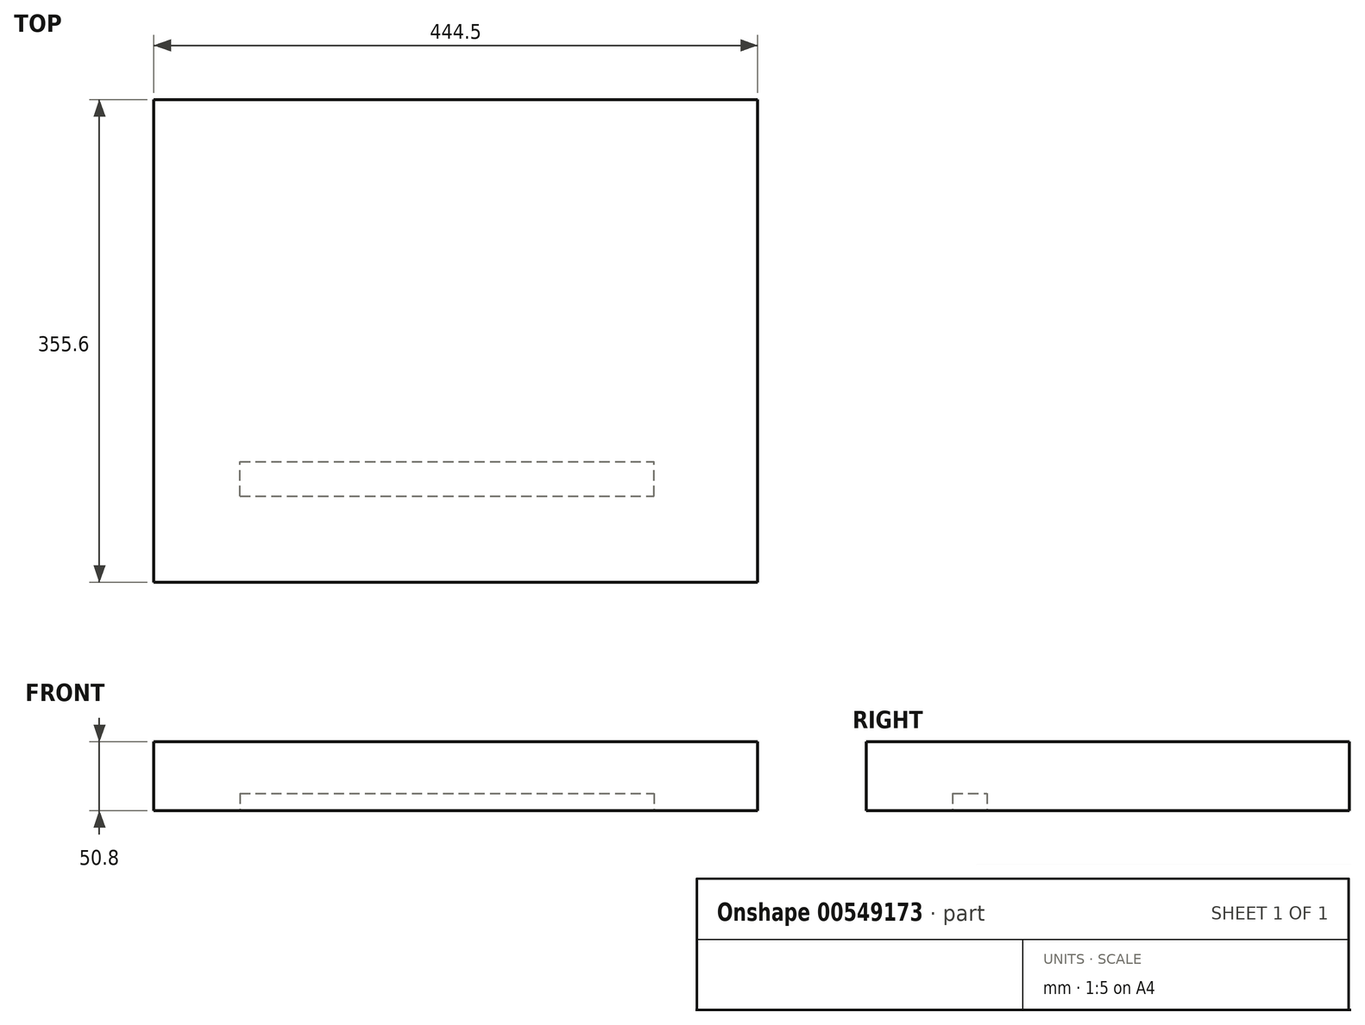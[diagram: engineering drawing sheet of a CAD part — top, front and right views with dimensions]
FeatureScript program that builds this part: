
annotation { "Feature Type Name" : "Feature", "Feature Type Description" : "" }
export const myFeature = defineFeature(function(context is Context, id is Id, definition is map)
    precondition{}
    {
        {
            var Q0;
            Q0=qCreatedBy(makeId("Top.planeOp"),FACE);
            var sketch = newSketch(context, id + "F0", { "sketchPlane" : qUnion([Q0])});
            skLineSegment(sketch, "E0.bottom", {"start": v(-222.25, 177.8) * mm, "end": v(222.25, 177.8) * mm});
            skLineSegment(sketch, "E0.top", {"start": v(-222.25, -177.8) * mm, "end": v(222.25, -177.8) * mm});
            skLineSegment(sketch, "E0.left", {"start": v(-222.25, 177.8) * mm, "end": v(-222.25, -177.8) * mm});
            skLineSegment(sketch, "E0.right", {"start": v(222.25, 177.8) * mm, "end": v(222.25, -177.8) * mm});
            skSolve(sketch);
        }
        {
            var Q0;
            Q0=makeQuery(id+"F0.imprint","IMPRINT",FACE,{"disambiguationData":[TD([[makeQuery(id+"F0.imprint","IMPRINT",EDGE,{"derivedFrom":sQuery(id+"F0.wireOp",EDGE,"E0.bottom")}),-1.0]])]});
            extrude(context, id + "F1", {"entities" : qUnion([Q0]), "depth" : 50.8 * mm, "offsetDistance" : 25.4 * mm});
        }
        {
            var Q0;
            Q0=makeQuery(id+"F0.imprint","IMPRINT",FACE,{"disambiguationData":[TD([[makeQuery(id+"F0.imprint","IMPRINT",EDGE,{"derivedFrom":sQuery(id+"F0.wireOp",EDGE,"E0.bottom")}),-1.0]])]});
            var sketch = newSketch(context, id + "F2", { "sketchPlane" : qUnion([Q0])});
            skLineSegment(sketch, "E1.bottom", {"start": v(-158.75, -114.3) * mm, "end": v(146.05, -114.3) * mm});
            skLineSegment(sketch, "E1.top", {"start": v(-158.75, -88.9) * mm, "end": v(146.05, -88.9) * mm});
            skLineSegment(sketch, "E1.left", {"start": v(-158.75, -114.3) * mm, "end": v(-158.75, -88.9) * mm});
            skLineSegment(sketch, "E1.right", {"start": v(146.05, -114.3) * mm, "end": v(146.05, -88.9) * mm});
            skSolve(sketch);
        }
        {
            var Q0;
            Q0 = qSketchRegion(id + "F2", true);
            extrude(context, id + "F3", {"entities" : qUnion([Q0]), "operationType" : NewBodyOperationType.REMOVE, "depth" : 12.7 * mm, "offsetDistance" : 25.4 * mm});
        }
    });
